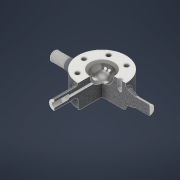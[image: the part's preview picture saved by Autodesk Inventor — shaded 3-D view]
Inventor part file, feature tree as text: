
AUTODESK INVENTOR PART (.ipt)
format: ipt  version: 2022 (Build 260153000, 153)  size: 319,488 bytes
history: native  units: mm
features: sketch x7, other x3, fillet x3, revolve x2, extrude x2, hole x2, thread x1, chamfer x1, mirror x1, pattern_circular x1
ambient origin geometry x8: Origin, YZ Plane, XZ Plane, XY Plane, X Axis, Y Axis, Z Axis, Center Point
bodies: Body1 (feature_tree)
feature tree (23):
  other  "Цилиндр1"
  other  "РабПлоскость1"
  revolve  "Вращение1"
  thread  "Резьба1"
  chamfer  "Фаска1"  Distance=100.0mm
  fillet  "Сопряжение1"  Radius=50.0mm
  mirror  "Зеркальное отражение1"
  other  "РабПлоскость3"
  extrude  "Выдавливание2"  Depth=100.0mm
  fillet  "Сопряжение2"  Radius=10.0mm
  fillet  "Сопряжение3"  Radius=30.0mm
  revolve  "Вращение2"
  hole  "Отверстие1"  [1 undecoded]
  hole  "Отверстие2"  [1 undecoded]
  pattern_circular  "Круговой массив1"  Angle=90.0deg  [1 undecoded]
  extrude  "Выдавливание3"  Depth=30.0mm TaperAngle=0.0deg
  sketch  "Эскиз5"
  sketch  "Эскиз6"
  sketch  "Эскиз9"
  sketch  "Эскиз10"
  sketch  "Эскиз15"
  sketch  "Эскиз16"
  sketch  "Эскиз17"
note: 3 required parameter values undecoded (feature->parameter linkage not recoverable at this tier; creation-order binding heuristic only, values carry confidence <= 0.55)
